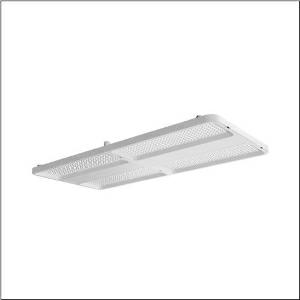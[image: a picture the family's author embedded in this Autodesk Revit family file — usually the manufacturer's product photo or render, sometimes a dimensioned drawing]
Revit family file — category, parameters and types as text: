
# Revit family: highbay_11_maxi_51hn12db4rda
name_source: partatom
category: Lighting Fixtures
units: mm (PartAtom-declared; Revit-internal decimal feet)

## family parameters
Cut with Voids When Loaded = No
Host = Face
Light Source = No
Part Type = Normal
Room Calculation Point = No
Round Connector Dimension = Use Diameter
Shared = No

## types (1)
- --- (1 x LED, 6720 lm, 32.8 W, 4000K)
    Apparent Load = 33 VA
    CIE Flux Codes = 87 98 100 100 100
    Color Rendering = 80
    Color Temperature = 4000K
    Default Elevation = 1800 mm
    Description = high bay luminaire Highbay 11 maxi; direct symmetric wide distribution, light control with lens of PMMA; UGR ≤ 22 (X = 4H | Y = 8H | S = 0.25H | reflection values 70/50/20); luminous flux: 42.500lm; light colour: 840, colour temperature: 4000K, MacAdam ≤ 2 SDCM (initial), colour rendering: CRI > 80; luminous efficacy: 198,9lm/W; rated service life: 100.000h (L95/B50) at AT= 25°C; control: DALI 2; housing frame of high-performance plastic PA6, matt traffic white (RAL 9016); cover of PMMA; dimension (LxWxH): 946 x 442 x 72mm; luminaire connection: terminal, 5-pole, max. 2.5mm² (cable entry for one cable, Ø 8.5..16mm); mains connection: 230..240V, AC/DC 0/50..60Hz; connected load: 213,7W; protection rating (complete): IP66; insulation class (complete): insulation class I (protective earthing); protection symbol: D; impact resistance: IK08; halogen-free wiring; for central battery installations according to DIN EN 60598-2-22; corresponds to IFS (International Featured Standards) requirements for safety and quality in the food industry; LABS conformity tested according to VDMA 24364:2018-05; certification: CE, ENEC, VDE, UKCA; permissible operating ambient temperature: -40..+50°C (reducing of maximum allowable ambient temperature of 5°C with ceiling mounting); packaging unit: 1 piece; (delivery without accessories; please order mounting accessories separately)
    Height = 72 mm  [stored 0.23622 ft]
    Lamp = 1 x LED
    Lamp Light Flux = 6720 lm
    Lamp Power = 32.8 W
    Lamp count = 1
    Length = 946 mm
    Luminous efficacy = 205 lm/W
    Manufacturer = Siteco
    ModVariant = No
    Model = 51HN12DB4RDA
    Mounting Place = Ceiling
    Mounting Type = Pendant
    Number of Poles = 1
    OnlyDefault = Yes
    Power Factor = 1
    Product Name = Highbay 11 maxi
    Product group = high bay luminaire
    ProductGroupID = 901
    Protection Class = Protection class I
    Protection Degree = IP 66
    RLX_Detail_Level = 1
    RLX_Emergency_Light_Flux = 0 lm
    RLX_Emergency_Type = 0
    RLX_Emergency_Type_DB = No
    RlxData = <blob elided: 22269 chars, md5=c4531e23>
    Socket = socket
    Standby Power = 0 W
    System Light Flux = 6720 lm
    System Power = 33 W
    Type Comments = : DC mode (central or group accumulator) initial emergency light level
    Type Image = l_1363244.jpg
    URL = http://relux.com
    VarID = @adj_005161
    Voltage = 0 V
    Weight = 0.00 kg
    Width = 442 mm

note: [stored X ft] marks values corroborated as IEEE doubles in the binary element streams (Revit-internal decimal feet)

## geometry (parser evidence)
native form markers: Blend x4, Sweep x11
no freeform markers — native parametric forms only
